# Revit family: Стандартнопроходной шаровой кран ВР-ВР
name_source: partatom
category: Арматура трубопроводов
revit_build: Autodesk Revit 2017 (Build: 20160225_1515(x64)
units: mm (PartAtom-declared; Revit-internal decimal feet)

## family parameters
Всегда вертикально = Да
На основе рабочей плоскости = Нет
Общий = Нет
При загрузке вырезать с полостями = Нет
Размер круглого соединителя = Использовать диаметр
Тип детали = Клапан - Вставляется

## types (5) — shared parameters
ADSK_Единица измерения = шт
ADSK_Завод-изготовитель = ООО САНЕКСТ.ПРО
ADSK_Материал наименование = DZR латунь
URL = http://sanext.ru
z = 1
Изготовитель = ООО САНЕКСТ.ПРО
Материал = DZR латунь
Рабочее давление = 0.00 кПа
Разработчик = ООО ПРОРУБИМ
Разработчик (телефон) = +7 (495) 649-85-43
Разработчик модели (URL) = http://prorubim.com
zero-valued in all types: ADSK_Масса, Коэффициент K

## per-type parameters (varying)
| type | ADSK_Код изделия | ADSK_Наименование | D1 | DN | D_нар | H | L | h_гайки | Описание | Ручка |
| DN40 | 8755 | Стандартнопроходной кран шаровой ВР-ВР DN40 | 14 мм | 40 мм | 52 мм | 66 мм | 88 мм | 13 мм | Стандартнопроходной кран шаровой ВР-ВР DN40 | Ручка крана |
| DN32 | 8754 | Стандартнопроходной кран шаровой ВР-ВР DN32 | 11 мм | 32 мм | 44 мм | 62 мм | 75 мм | 11 мм | Стандартнопроходной кран шаровой ВР-ВР DN32 | Ручка крана |
| DN25 | 8753 | Стандартнопроходной кран шаровой ВР-ВР DN25 | 9 мм | 25 мм | 37 мм | 52 мм | 63 мм | 9 мм | Стандартнопроходной кран шаровой ВР-ВР DN25 | Барашек на шаровой кран |
| DN20 | 8752 | Стандартнопроходной кран шаровой ВР-ВР DN20 | 7 мм | 20 мм | 32 мм | 44 мм | 54 мм | 8 мм | Стандартнопроходной кран шаровой ВР-ВР DN20 | Барашек на шаровой кран |
| DN15 | 8751 | Стандартнопроходной кран шаровой ВР-ВР DN15 | 5 мм | 15 мм | 27 мм | 41 мм | 47 мм | 7 мм | Стандартнопроходной кран шаровой ВР-ВР DN15 | Барашек на шаровой кран |
